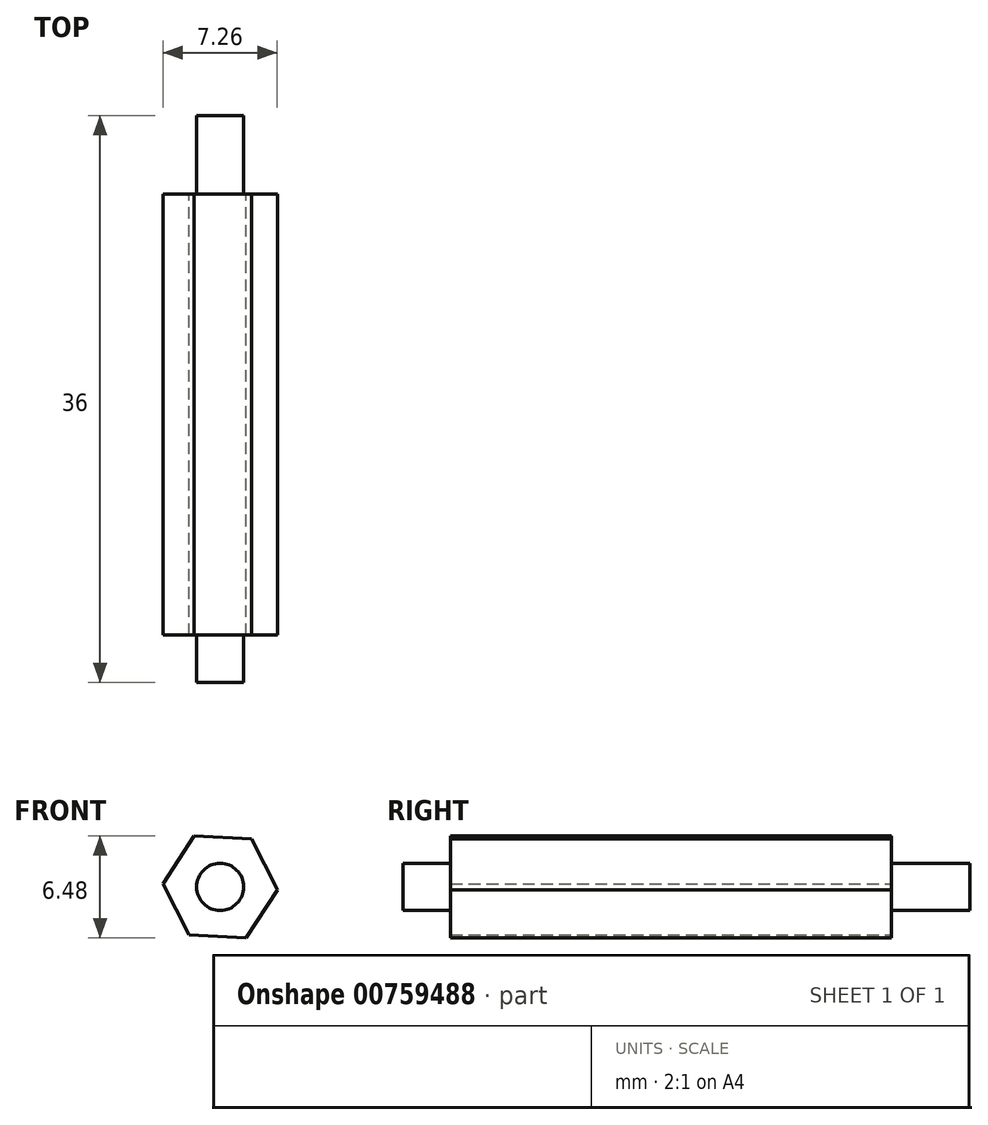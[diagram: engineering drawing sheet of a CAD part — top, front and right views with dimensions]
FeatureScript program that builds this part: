
annotation { "Feature Type Name" : "Feature", "Feature Type Description" : "" }
export const myFeature = defineFeature(function(context is Context, id is Id, definition is map)
    precondition{}
    {
        {
            var Q0;
            Q0=qCreatedBy(makeId("Front.planeOp"),FACE);
            var sketch = newSketch(context, id + "F0", { "sketchPlane" : qUnion([Q0])});
            skCircle(sketch, "E0.cCircle", {"center": v(0, 0) * mm, "radius": 3.15 * mm, "construction": true});
            skLineSegment(sketch, "E0.0", {"start": v(-1.98, -3.05) * mm, "end": v(-3.63, 0.2) * mm});
            skLineSegment(sketch, "E0.1", {"start": v(-3.63, 0.2) * mm, "end": v(-1.65, 3.24) * mm});
            skLineSegment(sketch, "E0.2", {"start": v(-1.65, 3.24) * mm, "end": v(1.98, 3.05) * mm});
            skLineSegment(sketch, "E0.3", {"start": v(1.98, 3.05) * mm, "end": v(3.63, -0.2) * mm});
            skLineSegment(sketch, "E0.4", {"start": v(3.63, -0.2) * mm, "end": v(1.65, -3.24) * mm});
            skLineSegment(sketch, "E0.5", {"start": v(1.65, -3.24) * mm, "end": v(-1.98, -3.05) * mm});
            skPoint(sketch, "E0.0.midPoint", {"position": v(-2.8, -1.43) * mm});
            skSolve(sketch);
        }
        {
            var Q0;
            Q0=makeQuery(id+"F0.imprint","IMPRINT",FACE,{"disambiguationData":[TD([[makeQuery(id+"F0.imprint","IMPRINT",EDGE,{"derivedFrom":sQuery(id+"F0.wireOp",EDGE,"E0.0")}),-1.0]])]});
            extrude(context, id + "F1", {"entities" : qUnion([Q0]), "depth" : 28 * mm, "offsetDistance" : 25 * mm});
        }
        {
            var Q0;
            Q0=makeQuery(id+"F1.opExtrude","CAP_FACE",FACE,{"disambiguationData":[OSD([sQuery(id+"F0.wireOp",EDGE,"E0.0"),sQuery(id+"F0.wireOp",EDGE,"E0.1"),sQuery(id+"F0.wireOp",EDGE,"E0.2"),sQuery(id+"F0.wireOp",EDGE,"E0.3"),sQuery(id+"F0.wireOp",EDGE,"E0.4"),sQuery(id+"F0.wireOp",EDGE,"E0.5")])],"isStart":false});
            var sketch = newSketch(context, id + "F2", { "sketchPlane" : qUnion([Q0])});
            skCircle(sketch, "E1", {"center": v(0, 0) * mm, "radius": 1.5 * mm});
            skSolve(sketch);
        }
        {
            var Q0;
            Q0 = qSketchRegion(id + "F2", true);
            extrude(context, id + "F3", {"entities" : qUnion([Q0]), "operationType" : NewBodyOperationType.ADD, "depth" : 3 * mm, "offsetDistance" : 25 * mm});
        }
        {
            var Q0;
            Q0=makeQuery(id+"F1.opExtrude","CAP_FACE",FACE,{"disambiguationData":[OSD([sQuery(id+"F0.wireOp",EDGE,"E0.0"),sQuery(id+"F0.wireOp",EDGE,"E0.1"),sQuery(id+"F0.wireOp",EDGE,"E0.2"),sQuery(id+"F0.wireOp",EDGE,"E0.3"),sQuery(id+"F0.wireOp",EDGE,"E0.4"),sQuery(id+"F0.wireOp",EDGE,"E0.5")])],"isStart":true});
            var sketch = newSketch(context, id + "F4", { "sketchPlane" : qUnion([Q0])});
            skCircle(sketch, "E2", {"center": v(0, 0) * mm, "radius": 1.5 * mm});
            skSolve(sketch);
        }
        {
            var Q0;
            Q0 = qSketchRegion(id + "F4", true);
            extrude(context, id + "F5", {"entities" : qUnion([Q0]), "operationType" : NewBodyOperationType.ADD, "depth" : 5 * mm, "offsetDistance" : 25 * mm});
        }
    });
